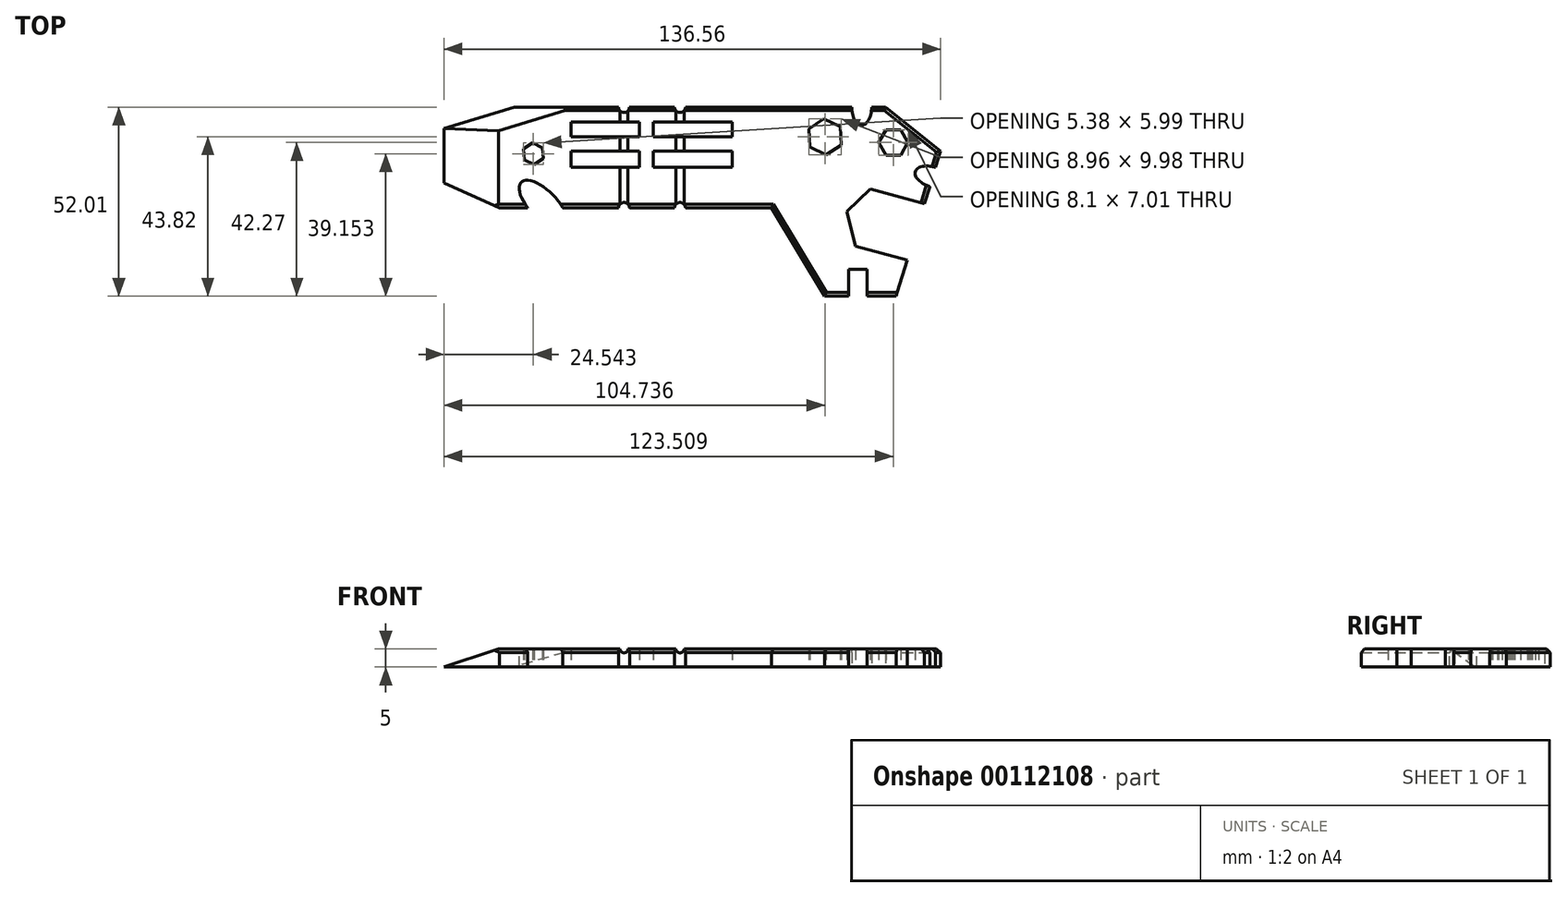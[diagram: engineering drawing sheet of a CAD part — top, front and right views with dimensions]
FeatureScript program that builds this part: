
annotation { "Feature Type Name" : "Feature", "Feature Type Description" : "" }
export const myFeature = defineFeature(function(context is Context, id is Id, definition is map)
    precondition{}
    {
        {
            var Q0;
            Q0=qCreatedBy(makeId("Top.planeOp"),FACE);
            var sketch = newSketch(context, id + "F0", { "sketchPlane" : qUnion([Q0])});
            skLineSegment(sketch, "E0", {"start": v(-45.59, 27.76) * mm, "end": v(-16.9, 27.76) * mm});
            skLineSegment(sketch, "E1", {"start": v(56.5, 27.76) * mm, "end": v(71.7, 15.68) * mm});
            skLineSegment(sketch, "E2", {"start": v(71.7, 15.68) * mm, "end": v(70.3, 11.16) * mm});
            skLineSegment(sketch, "E3", {"start": v(59.42, -24.25) * mm, "end": v(51.42, -24.25) * mm});
            skLineSegment(sketch, "E4", {"start": v(51.42, -24.25) * mm, "end": v(51.42, -20.36) * mm});
            skLineSegment(sketch, "E5", {"start": v(54.02, -16.85) * mm, "end": v(49.73, -16.85) * mm});
            skLineSegment(sketch, "E6", {"start": v(46.42, -20.36) * mm, "end": v(46.42, -24.25) * mm});
            skLineSegment(sketch, "E7", {"start": v(46.42, -24.25) * mm, "end": v(39.74, -24.25) * mm});
            skLineSegment(sketch, "E8", {"start": v(39.74, -24.25) * mm, "end": v(25.13, 0) * mm});
            skLineSegment(sketch, "E9", {"start": v(25.13, 0) * mm, "end": v(1.5, 0) * mm});
            skLineSegment(sketch, "E10", {"start": v(-34.1, 0) * mm, "end": v(-49.68, 0) * mm});
            skLineSegment(sketch, "E11", {"start": v(-49.68, 0) * mm, "end": v(-64.87, 6.92) * mm});
            skLineSegment(sketch, "E12", {"start": v(-64.87, 6.92) * mm, "end": v(-64.87, 21.92) * mm});
            skLineSegment(sketch, "E13", {"start": v(-64.87, 21.92) * mm, "end": v(-45.59, 27.76) * mm});
            skLineSegment(sketch, "E14.bottom", {"start": v(-7.4, 23.67) * mm, "end": v(14.42, 23.67) * mm});
            skLineSegment(sketch, "E14.top", {"start": v(-7.4, 19.58) * mm, "end": v(14.42, 19.58) * mm});
            skLineSegment(sketch, "E14.left", {"start": v(-7.4, 23.67) * mm, "end": v(-7.4, 19.58) * mm});
            skLineSegment(sketch, "E14.right", {"start": v(14.42, 23.67) * mm, "end": v(14.42, 19.58) * mm});
            skLineSegment(sketch, "E15.bottom", {"start": v(-11.1, 23.67) * mm, "end": v(-30, 23.67) * mm});
            skLineSegment(sketch, "E15.top", {"start": v(-11.1, 19.58) * mm, "end": v(-30, 19.58) * mm});
            skLineSegment(sketch, "E15.left", {"start": v(-11.1, 23.67) * mm, "end": v(-11.1, 19.58) * mm});
            skLineSegment(sketch, "E15.right", {"start": v(-30, 23.67) * mm, "end": v(-30, 19.58) * mm});
            skLineSegment(sketch, "E16.bottom", {"start": v(-7.4, 15.68) * mm, "end": v(14.42, 15.68) * mm});
            skLineSegment(sketch, "E16.top", {"start": v(-7.4, 11.2) * mm, "end": v(14.42, 11.2) * mm});
            skLineSegment(sketch, "E16.left", {"start": v(-7.4, 15.68) * mm, "end": v(-7.4, 11.2) * mm});
            skLineSegment(sketch, "E16.right", {"start": v(14.42, 15.68) * mm, "end": v(14.42, 11.2) * mm});
            skCircle(sketch, "E17.cCircle", {"center": v(58.64, 18.02) * mm, "radius": 3.5 * mm, "construction": true});
            skLineSegment(sketch, "E17.0", {"start": v(60.66, 14.51) * mm, "end": v(56.61, 14.51) * mm});
            skLineSegment(sketch, "E17.1", {"start": v(56.61, 14.51) * mm, "end": v(54.6, 18.02) * mm});
            skLineSegment(sketch, "E17.2", {"start": v(54.6, 18.02) * mm, "end": v(56.61, 21.53) * mm});
            skLineSegment(sketch, "E17.3", {"start": v(56.61, 21.53) * mm, "end": v(60.66, 21.53) * mm});
            skLineSegment(sketch, "E17.4", {"start": v(60.66, 21.53) * mm, "end": v(62.69, 18.02) * mm});
            skLineSegment(sketch, "E17.5", {"start": v(62.69, 18.02) * mm, "end": v(60.66, 14.51) * mm});
            skPoint(sketch, "E17.0.midPoint", {"position": v(58.64, 14.51) * mm});
            skCircle(sketch, "E18.cCircle", {"center": v(39.87, 19.57) * mm, "radius": 4.33 * mm, "construction": true});
            skLineSegment(sketch, "E18.0", {"start": v(44.35, 17.35) * mm, "end": v(40.19, 14.58) * mm});
            skLineSegment(sketch, "E18.1", {"start": v(40.19, 14.58) * mm, "end": v(35.7, 16.8) * mm});
            skLineSegment(sketch, "E18.2", {"start": v(35.7, 16.8) * mm, "end": v(35.38, 21.79) * mm});
            skLineSegment(sketch, "E18.3", {"start": v(35.38, 21.79) * mm, "end": v(39.54, 24.56) * mm});
            skLineSegment(sketch, "E18.4", {"start": v(39.54, 24.56) * mm, "end": v(44.03, 22.34) * mm});
            skLineSegment(sketch, "E18.5", {"start": v(44.03, 22.34) * mm, "end": v(44.35, 17.35) * mm});
            skPoint(sketch, "E18.0.midPoint", {"position": v(42.27, 15.97) * mm});
            skCircle(sketch, "E19.cCircle", {"center": v(-40.33, 14.9) * mm, "radius": 2.6 * mm, "construction": true});
            skLineSegment(sketch, "E19.0", {"start": v(-37.64, 13.57) * mm, "end": v(-40.13, 11.9) * mm});
            skLineSegment(sketch, "E19.1", {"start": v(-40.13, 11.9) * mm, "end": v(-42.82, 13.24) * mm});
            skLineSegment(sketch, "E19.2", {"start": v(-42.82, 13.24) * mm, "end": v(-43.02, 16.23) * mm});
            skLineSegment(sketch, "E19.3", {"start": v(-43.02, 16.23) * mm, "end": v(-40.52, 17.9) * mm});
            skLineSegment(sketch, "E19.4", {"start": v(-40.52, 17.9) * mm, "end": v(-37.83, 16.57) * mm});
            skLineSegment(sketch, "E19.5", {"start": v(-37.83, 16.57) * mm, "end": v(-37.64, 13.57) * mm});
            skPoint(sketch, "E19.0.midPoint", {"position": v(-38.89, 12.74) * mm});
            skArc(sketch, "E20", {"start": v(-13.9, 0) * mm, "mid": v(-15.4, 1.5) * mm, "end": v(-16.9, 0) * mm});
            skArc(sketch, "E21", {"start": v(-16.9, 27.76) * mm, "mid": v(-15.4, 26.26) * mm, "end": v(-13.9, 27.76) * mm});
            skArc(sketch, "E22", {"start": v(-1.5, 27.76) * mm, "mid": v(0, 26.26) * mm, "end": v(1.5, 27.76) * mm});
            skArc(sketch, "E23", {"start": v(1.5, 0) * mm, "mid": v(0, 1.5) * mm, "end": v(-1.5, 0) * mm});
            skLineSegment(sketch, "E24.trimOffspring", {"start": v(-13.9, 27.76) * mm, "end": v(-1.5, 27.76) * mm});
            skLineSegment(sketch, "E25.trimOffspring", {"start": v(1.5, 27.76) * mm, "end": v(47.2, 27.76) * mm});
            skLineSegment(sketch, "E26.trimOffspring", {"start": v(-1.5, 0) * mm, "end": v(-13.9, 0) * mm});
            skLineSegment(sketch, "E27.trimOffspring", {"start": v(-16.9, 0) * mm, "end": v(-19.68, 0) * mm});
            skLineSegment(sketch, "E28", {"start": v(46.42, -20.36) * mm, "end": v(46.42, -16.85) * mm});
            skLineSegment(sketch, "E29", {"start": v(46.42, -16.85) * mm, "end": v(51.42, -16.85) * mm});
            skLineSegment(sketch, "E30", {"start": v(51.42, -16.85) * mm, "end": v(51.42, -20.36) * mm});
            skLineSegment(sketch, "E31.trimOffspring", {"start": v(52.7, 27.76) * mm, "end": v(56.5, 27.76) * mm});
            skLineSegment(sketch, "E32.trimOffspring", {"start": v(68.69, 5.9) * mm, "end": v(67.22, 1.14) * mm});
            skEllipticalArc(sketch, "E33", {});
            skEllipticalArc(sketch, "E34", {});
            skPoint(sketch, "E35.orphan", {"position": v(51.45, 27.76) * mm});
            skPoint(sketch, "E36.orphan", {"position": v(48.45, 27.76) * mm});
            skPoint(sketch, "E37.orphan", {"position": v(69.94, 9.97) * mm});
            skPoint(sketch, "E38.orphan", {"position": v(69.05, 7.1) * mm});
            skLineSegment(sketch, "E39", {"start": v(-19.68, 0) * mm, "end": v(-34.1, 0) * mm});
            skLineSegment(sketch, "E40.1", {"start": v(49.4, -10.76) * mm, "end": v(48.32, -10.46) * mm});
            skLineSegment(sketch, "E40.2", {"start": v(48.32, -10.46) * mm, "end": v(45.89, -1.04) * mm});
            skLineSegment(sketch, "E40.3", {"start": v(45.89, -1.04) * mm, "end": v(52.32, 5.28) * mm});
            skLineSegment(sketch, "E40.4", {"start": v(52.32, 5.28) * mm, "end": v(54.9, 4.56) * mm});
            skPoint(sketch, "E40.0.midPoint", {"position": v(53.6, -6.63) * mm});
            skLineSegment(sketch, "E41", {"start": v(54.9, 4.56) * mm, "end": v(67.22, 1.14) * mm});
            skLineSegment(sketch, "E42", {"start": v(49.4, -10.76) * mm, "end": v(62.45, -14.38) * mm});
            skLineSegment(sketch, "E43.trimOffspring", {"start": v(62.45, -14.38) * mm, "end": v(59.42, -24.25) * mm});
            skPoint(sketch, "E44.orphan", {"position": v(57.8, -2.5) * mm});
            skPoint(sketch, "E40.cCircle.center.orphan", {"position": v(61.52, 0) * mm});
            skLineSegment(sketch, "E45.bottom", {"start": v(-11.1, 15.68) * mm, "end": v(-30, 15.68) * mm});
            skLineSegment(sketch, "E45.top", {"start": v(-11.1, 11.2) * mm, "end": v(-30, 11.2) * mm});
            skLineSegment(sketch, "E45.left", {"start": v(-11.1, 15.68) * mm, "end": v(-11.1, 11.2) * mm});
            skLineSegment(sketch, "E45.right", {"start": v(-30, 15.68) * mm, "end": v(-30, 11.2) * mm});
            const initialGuessF0  = {"E33": [0.06949467194268627, 0.008533030497793153, 0.9563239555464013, -0.29230889833887175, 0.005, 0.00275, 1.5699626169969383, 4.711555270586743], "E34": [0.04994562640786171, 0.02776037058447559, 0, -1, 0.005, 0.00275, 4.71238898038469, 1.5707963267948966]};
            skSetInitialGuess(sketch, initialGuessF0);
            skSolve(sketch);
        }
        {
            var Q0;
            Q0 = qSketchRegion(id + "F0", true);
            var Q1;
            Q1=makeQuery(id+"F0.imprint","IMPRINT",FACE,{"disambiguationData":[TD([[makeQuery(id+"F0.imprint","IMPRINT",EDGE,{"derivedFrom":sQuery(id+"F0.wireOp",EDGE,"E0")}),-1.0]])]});
            extrude(context, id + "F1", {"entities" : qUnion([Q0, Q1]), "depth" : 5 * mm});
        }
        {
            var Q0;
            Q0=makeQuery(id+"F1.opExtrude","CAP_EDGE",EDGE,{"disambiguationData":[OSD([sQuery(id+"F0.wireOp",EDGE,"E12")])],"isStart":false});
            chamfer(context, id + "F2", {"entities" : qUnion([Q0]), "chamferType" : ChamferType.TWO_OFFSETS, "width1" : 5 * mm, "oppositeDirection" : false, "width2" : 15 * mm, "tangentPropagation" : true});
        }
        {
            var Q0;
            Q0=makeQuery(id+"F1.opExtrude","CAP_EDGE",EDGE,{"disambiguationData":[OSD([sQuery(id+"F0.wireOp",EDGE,"E9")])],"isStart":false});
            var Q1;
            Q1=makeQuery(id+"F1.opExtrude","CAP_EDGE",EDGE,{"disambiguationData":[OSD([sQuery(id+"F0.wireOp",EDGE,"E26.trimOffspring")])],"isStart":false});
            var Q2;
            Q2=makeQuery(id+"F1.opExtrude","CAP_EDGE",EDGE,{"disambiguationData":[OSD([sQuery(id+"F0.wireOp",EDGE,"E24.trimOffspring")])],"isStart":false});
            var Q3;
            Q3=makeQuery(id+"F1.opExtrude","CAP_EDGE",EDGE,{"disambiguationData":[OSD([sQuery(id+"F0.wireOp",EDGE,"E25.trimOffspring")])],"isStart":false});
            var Q4;
            Q4=makeQuery(id+"F1.opExtrude","CAP_EDGE",EDGE,{"disambiguationData":[OSD([sQuery(id+"F0.wireOp",EDGE,"E0")])],"isStart":false});
            var Q5;
            Q5=makeQuery(id+"F1.opExtrude","CAP_EDGE",EDGE,{"disambiguationData":[OSD([sQuery(id+"F0.wireOp",EDGE,"E8")])],"isStart":false});
            var Q6;
            Q6=makeQuery(id+"F1.opExtrude","CAP_EDGE",EDGE,{"disambiguationData":[OSD([sQuery(id+"F0.wireOp",EDGE,"E32.trimOffspring")])],"isStart":false});
            var Q7;
            Q7=makeQuery(id+"F1.opExtrude","CAP_EDGE",EDGE,{"disambiguationData":[OSD([sQuery(id+"F0.wireOp",EDGE,"E1")])],"isStart":false});
            var Q8;
            Q8=makeQuery(id+"F1.opExtrude","CAP_EDGE",EDGE,{"disambiguationData":[OSD([sQuery(id+"F0.wireOp",EDGE,"E2")])],"isStart":false});
            var Q9;
            Q9=makeQuery(id+"F1.opExtrude","CAP_EDGE",EDGE,{"disambiguationData":[OSD([sQuery(id+"F0.wireOp",EDGE,"E31.trimOffspring")])],"isStart":false});
            var Q10;
            Q10=makeQuery(id+"F1.opExtrude","CAP_EDGE",EDGE,{"disambiguationData":[OSD([sQuery(id+"F0.wireOp",EDGE,"E3")])],"isStart":false});
            var Q11;
            Q11=makeQuery(id+"F1.opExtrude","CAP_EDGE",EDGE,{"disambiguationData":[OSD([sQuery(id+"F0.wireOp",EDGE,"E7")])],"isStart":false});
            var Q12;
            Q12=makeQuery(id+"F1.opExtrude","CAP_EDGE",EDGE,{"disambiguationData":[OSD([sQuery(id+"F0.wireOp",EDGE,"E27.trimOffspring")])],"isStart":false});
            var Q13;
            Q13=makeQuery(id+"F1.opExtrude","CAP_EDGE",EDGE,{"disambiguationData":[OSD([sQuery(id+"F0.wireOp",EDGE,"E10")])],"isStart":false});
            chamfer(context, id + "F3", {"entities" : qUnion([Q0, Q1, Q2, Q3, Q4, Q5, Q6, Q7, Q8, Q9, Q10, Q11, Q12, Q13]), "width" : 1 * mm, "tangentPropagation" : true});
        }
        {
            var Q0;
            Q0=makeQuery(id+"F1.opExtrude","CAP_EDGE",EDGE,{"disambiguationData":[OSD([sQuery(id+"F0.wireOp",EDGE,"E13")])],"isStart":false});
            chamfer(context, id + "F4", {"entities" : qUnion([Q0]), "chamferType" : ChamferType.TWO_OFFSETS, "width1" : 5 * mm, "oppositeDirection" : false, "width2" : 5 * mm, "tangentPropagation" : true});
        }
        {
            var Q0;
            Q0=makeQuery(id+"F1.opExtrude","SWEPT_FACE",FACE,{"disambiguationData":[OSD([sQuery(id+"F0.wireOp",EDGE,"E10"),sQuery(id+"F0.wireOp",EDGE,"E27.trimOffspring"),sQuery(id+"F0.wireOp",EDGE,"E39")])]});
            var sketch = newSketch(context, id + "F5", { "sketchPlane" : qUnion([Q0])});
            skLineSegment(sketch, "E46.0", {"start": v(-14.27, 5) * mm, "end": v(-16.5, 5) * mm});
            skLineSegment(sketch, "E47.0", {"start": v(1.12, 5) * mm, "end": v(-1.12, 5) * mm});
            skCircle(sketch, "E48", {"center": v(-15.4, 5) * mm, "radius": 1.12 * mm});
            skCircle(sketch, "E49", {"center": v(0, 5) * mm, "radius": 1.12 * mm});
            skSolve(sketch);
        }
        {
            var Q0;
            Q0 = qSketchRegion(id + "F5", true);
            extrude(context, id + "F6", {"entities" : qUnion([Q0]), "operationType" : NewBodyOperationType.REMOVE, "endBound" : BoundingType.THROUGH_ALL, "oppositeDirection" : true, "depth" : 25 * mm});
        }
        {
            var Q0;
            {var subQ0=sQuery(id+"F0.wireOp",EDGE,"E19.5");var subQ1=sQuery(id+"F0.wireOp",EDGE,"E19.4");var subQ2=sQuery(id+"F0.wireOp",EDGE,"E13");var subQ3=sQuery(id+"F0.wireOp",EDGE,"E20");var subQ4=sQuery(id+"F0.wireOp",EDGE,"E19.3");var subQ5=sQuery(id+"F0.wireOp",EDGE,"E19.1");var subQ6=sQuery(id+"F0.wireOp",EDGE,"E15.top");var subQ7=sQuery(id+"F0.wireOp",EDGE,"E15.bottom");var subQ8=sQuery(id+"F0.wireOp",EDGE,"E19.0");var subQ9=sQuery(id+"F0.wireOp",EDGE,"E15.right");var subQ10=sQuery(id+"F0.wireOp",EDGE,"E21");var subQ11=sQuery(id+"F0.wireOp",EDGE,"E19.2");var subQ12=sQuery(id+"F0.wireOp",EDGE,"E45.right");var subQ13=sQuery(id+"F0.wireOp",EDGE,"E45.bottom");var subQ14=sQuery(id+"F0.wireOp",EDGE,"E0");var subQ15=sQuery(id+"F0.wireOp",EDGE,"E45.top");var subQ16=sQuery(id+"F0.wireOp",EDGE,"E12");var subQ17=sQuery(id+"F0.wireOp",EDGE,"E39");var subQ18=sQuery(id+"F0.wireOp",EDGE,"E27.trimOffspring");var subQ19=sQuery(id+"F0.wireOp",EDGE,"E10");Q0=makeQuery(id+"F6.boolean.opBoolean","SPLIT",FACE,{"disambiguationData":[TD([makeQuery(id+"F1.opExtrude","SWEPT_FACE",FACE,{"disambiguationData":[OSD([subQ9])]})])],"derivedFrom":makeQuery(id+"F1.opExtrude","CAP_FACE",FACE,{"disambiguationData":[OSD([subQ14,sQuery(id+"F0.wireOp",EDGE,"E1"),sQuery(id+"F0.wireOp",EDGE,"E2"),sQuery(id+"F0.wireOp",EDGE,"E3"),sQuery(id+"F0.wireOp",EDGE,"E4"),sQuery(id+"F0.wireOp",EDGE,"E6"),sQuery(id+"F0.wireOp",EDGE,"E7"),sQuery(id+"F0.wireOp",EDGE,"E8"),sQuery(id+"F0.wireOp",EDGE,"E9"),subQ19,sQuery(id+"F0.wireOp",EDGE,"E11"),subQ16,subQ2,sQuery(id+"F0.wireOp",EDGE,"E14.bottom"),sQuery(id+"F0.wireOp",EDGE,"E14.top"),sQuery(id+"F0.wireOp",EDGE,"E14.left"),sQuery(id+"F0.wireOp",EDGE,"E14.right"),subQ7,subQ6,sQuery(id+"F0.wireOp",EDGE,"E15.left"),subQ9,sQuery(id+"F0.wireOp",EDGE,"E16.bottom"),sQuery(id+"F0.wireOp",EDGE,"E16.top"),sQuery(id+"F0.wireOp",EDGE,"E16.left"),sQuery(id+"F0.wireOp",EDGE,"E16.right"),sQuery(id+"F0.wireOp",EDGE,"E17.0"),sQuery(id+"F0.wireOp",EDGE,"E17.1"),sQuery(id+"F0.wireOp",EDGE,"E17.2"),sQuery(id+"F0.wireOp",EDGE,"E17.3"),sQuery(id+"F0.wireOp",EDGE,"E17.4"),sQuery(id+"F0.wireOp",EDGE,"E17.5"),sQuery(id+"F0.wireOp",EDGE,"E18.0"),sQuery(id+"F0.wireOp",EDGE,"E18.1"),sQuery(id+"F0.wireOp",EDGE,"E18.2"),sQuery(id+"F0.wireOp",EDGE,"E18.3"),sQuery(id+"F0.wireOp",EDGE,"E18.4"),sQuery(id+"F0.wireOp",EDGE,"E18.5"),subQ8,subQ5,subQ11,subQ4,subQ1,subQ0,subQ3,subQ10,sQuery(id+"F0.wireOp",EDGE,"E22"),sQuery(id+"F0.wireOp",EDGE,"E23"),sQuery(id+"F0.wireOp",EDGE,"E24.trimOffspring"),sQuery(id+"F0.wireOp",EDGE,"E25.trimOffspring"),sQuery(id+"F0.wireOp",EDGE,"E26.trimOffspring"),subQ18,sQuery(id+"F0.wireOp",EDGE,"E28"),sQuery(id+"F0.wireOp",EDGE,"E29"),sQuery(id+"F0.wireOp",EDGE,"E30"),sQuery(id+"F0.wireOp",EDGE,"E31.trimOffspring"),sQuery(id+"F0.wireOp",EDGE,"E32.trimOffspring"),sQuery(id+"F0.wireOp",EDGE,"E33"),sQuery(id+"F0.wireOp",EDGE,"E34"),subQ17,sQuery(id+"F0.wireOp",EDGE,"E40.1"),sQuery(id+"F0.wireOp",EDGE,"E40.2"),sQuery(id+"F0.wireOp",EDGE,"E40.3"),sQuery(id+"F0.wireOp",EDGE,"E40.4"),sQuery(id+"F0.wireOp",EDGE,"E41"),sQuery(id+"F0.wireOp",EDGE,"E42"),sQuery(id+"F0.wireOp",EDGE,"E43.trimOffspring"),subQ13,subQ15,sQuery(id+"F0.wireOp",EDGE,"E45.left"),subQ12])],"isStart":false})});}
            var sketch = newSketch(context, id + "F7", { "sketchPlane" : qUnion([Q0])});
            skEllipse(sketch, "E50", {"center": v(-37.68, 1) * mm, "majorRadius": 8.49 * mm, "minorRadius": 3.78 * mm, "majorAxis": v(-0.7, 0.71)});
            skSolve(sketch);
        }
        {
            var Q0;
            Q0 = qSketchRegion(id + "F7", true);
            extrude(context, id + "F8", {"entities" : qUnion([Q0]), "operationType" : NewBodyOperationType.REMOVE, "oppositeDirection" : true, "depth" : 25 * mm});
        }
    });
